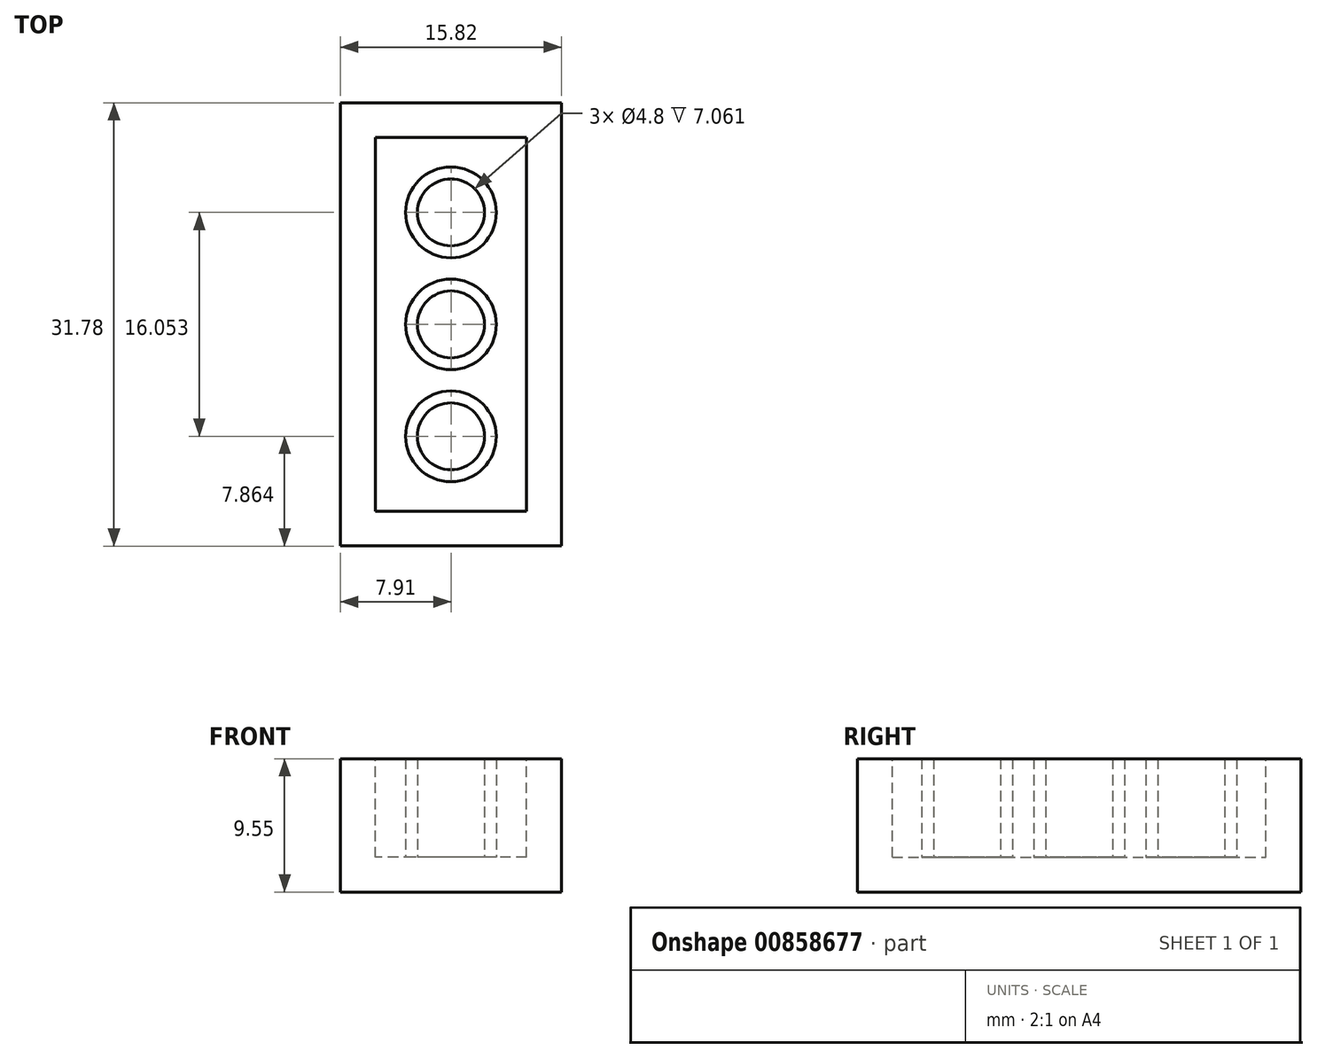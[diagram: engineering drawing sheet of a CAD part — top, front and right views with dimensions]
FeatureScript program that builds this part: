
annotation { "Feature Type Name" : "Feature", "Feature Type Description" : "" }
export const myFeature = defineFeature(function(context is Context, id is Id, definition is map)
    precondition{}
    {
        {
            var Q0;
            Q0=qCreatedBy(makeId("Right.planeOp"),FACE);
            var sketch = newSketch(context, id + "F0", { "sketchPlane" : qUnion([Q0])});
            skLineSegment(sketch, "E0.bottom", {"start": v(0, 0) * mm, "end": v(15.89, 0) * mm});
            skLineSegment(sketch, "E0.top", {"start": v(0, 9.55) * mm, "end": v(15.89, 9.55) * mm});
            skLineSegment(sketch, "E0.left", {"start": v(0, 0) * mm, "end": v(0, 9.55) * mm});
            skLineSegment(sketch, "E0.right", {"start": v(15.89, 0) * mm, "end": v(15.89, 9.55) * mm});
            skSolve(sketch);
        }
        {
            var Q0;
            Q0=makeQuery(id+"F0.imprint","IMPRINT",FACE,{"disambiguationData":[TD([[makeQuery(id+"F0.imprint","IMPRINT",EDGE,{"derivedFrom":sQuery(id+"F0.wireOp",EDGE,"E0.bottom")}),1.0]])]});
            extrude(context, id + "F1", {"entities" : qUnion([Q0]), "offsetDistance" : 25.4 * mm, "depth" : 7.9 * mm});
        }
        {
            var Q0;
            Q0=makeQuery(id+"F1.opExtrude","SWEPT_BODY",BODY,{"disambiguationData":[OSD([sQuery(id+"F0.wireOp",EDGE,"E0.bottom"),sQuery(id+"F0.wireOp",EDGE,"E0.top"),sQuery(id+"F0.wireOp",EDGE,"E0.left"),sQuery(id+"F0.wireOp",EDGE,"E0.right")])]});
            var Q1;
            Q1=qCreatedBy(makeId("Front.planeOp"),FACE);
            mirror(context, id + "F2", {"operationType" : NewBodyOperationType.ADD, "entities" : qUnion([Q0]), "mirrorPlane" : qUnion([Q1])});
        }
        {
            var Q0;
            Q0=makeQuery(id+"F1.opExtrude","SWEPT_BODY",BODY,{"disambiguationData":[OSD([sQuery(id+"F0.wireOp",EDGE,"E0.bottom"),sQuery(id+"F0.wireOp",EDGE,"E0.top"),sQuery(id+"F0.wireOp",EDGE,"E0.left"),sQuery(id+"F0.wireOp",EDGE,"E0.right")])]});
            var Q1;
            Q1=qCreatedBy(makeId("Right.planeOp"),FACE);
            mirror(context, id + "F3", {"operationType" : NewBodyOperationType.ADD, "entities" : qUnion([Q0]), "mirrorPlane" : qUnion([Q1])});
        }
        {
            var Q0;
            {var subQ0=makeQuery(id+"F1.opExtrude","SWEPT_FACE",FACE,{"disambiguationData":[OSD([sQuery(id+"F0.wireOp",EDGE,"E0.top")])]});var subQ1=makeQuery(id+"F2.boolean.opBoolean","MERGE",FACE,{"derivedFrom":[subQ0,makeQuery(id+"F2.opPattern","COPY",FACE,{"derivedFrom":subQ0,"instanceName":"1"})]});Q0=makeQuery(id+"F3.boolean.opBoolean","MERGE",FACE,{"derivedFrom":[subQ1,makeQuery(id+"F3.opPattern","COPY",FACE,{"derivedFrom":subQ1,"instanceName":"1"})]});}
            shell(context, id + "F4", {"entities" : qUnion([Q0]), "thickness" : 2.5 * mm});
        }
        {
            var Q0;
            Q0=makeQuery(id+"F4.opShell","OFFSET_FACE",FACE,{"disambiguationData":[OSD([sQuery(id+"F0.wireOp",EDGE,"E0.bottom")])]});
            var sketch = newSketch(context, id + "F5", { "sketchPlane" : qUnion([Q0])});
            skCircle(sketch, "E1", {"center": v(0, 0) * mm, "radius": 2.4 * mm});
            skCircle(sketch, "E2", {"center": v(0, 8.03) * mm, "radius": 2.4 * mm});
            skCircle(sketch, "E3", {"center": v(0, -8.03) * mm, "radius": 2.4 * mm});
            skCircle(sketch, "E4", {"center": v(0, -8.03) * mm, "radius": 3.25 * mm});
            skCircle(sketch, "E5", {"center": v(0, 0) * mm, "radius": 3.25 * mm});
            skCircle(sketch, "E6", {"center": v(0, 8.03) * mm, "radius": 3.25 * mm});
            skSolve(sketch);
        }
        {
            var Q0;
            Q0=makeQuery(id+"F5.imprint","IMPRINT",FACE,{"disambiguationData":[TD([[makeQuery(id+"F5.imprint","IMPRINT",EDGE,{"derivedFrom":sQuery(id+"F5.wireOp",EDGE,"E3")}),-1.0]])]});
            var Q1;
            Q1=makeQuery(id+"F5.imprint","IMPRINT",FACE,{"disambiguationData":[TD([[makeQuery(id+"F5.imprint","IMPRINT",EDGE,{"derivedFrom":sQuery(id+"F5.wireOp",EDGE,"E1")}),-1.0]])]});
            var Q2;
            Q2=makeQuery(id+"F5.imprint","IMPRINT",FACE,{"disambiguationData":[TD([[makeQuery(id+"F5.imprint","IMPRINT",EDGE,{"derivedFrom":sQuery(id+"F5.wireOp",EDGE,"E2")}),-1.0]])]});
            var Q3;
            {var subQ0=makeQuery(id+"F1.opExtrude","SWEPT_FACE",FACE,{"disambiguationData":[OSD([sQuery(id+"F0.wireOp",EDGE,"E0.top")])]});var subQ1=makeQuery(id+"F2.boolean.opBoolean","MERGE",FACE,{"derivedFrom":[subQ0,makeQuery(id+"F2.opPattern","COPY",FACE,{"derivedFrom":subQ0,"instanceName":"1"})]});Q3=makeQuery(id+"F3.boolean.opBoolean","MERGE",FACE,{"derivedFrom":[subQ1,makeQuery(id+"F3.opPattern","COPY",FACE,{"derivedFrom":subQ1,"instanceName":"1"})]});}
            extrude(context, id + "F6", {"entities" : qUnion([Q0, Q1, Q2]), "operationType" : NewBodyOperationType.ADD, "endBound" : BoundingType.UP_TO_SURFACE, "endBoundEntityFace" : qUnion([Q3]), "depth" : 25.4 * mm});
        }
    });
